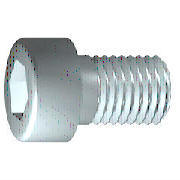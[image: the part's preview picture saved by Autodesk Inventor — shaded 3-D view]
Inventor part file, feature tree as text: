
AUTODESK INVENTOR PART (.ipt)
format: ipt  version: 2024 (Build 280153000, 153)  size: 186,368 bytes
history: native  units: mm (DEFAULTED — no unit token found)
features: extrude x1, plane x1, fillet x1
ambient origin geometry x7: Origin, YZ Plane, XY Plane, X Axis, Y Axis, Z Axis, Center Point
bodies: Solid1 (feature_tree), Body (feature_tree)
feature tree (3):
  extrude  "Slot"  Depth=18.0mm
  plane  "Work Plane1"
  fillet  "Fillet2"  Radius=0.306825mm
